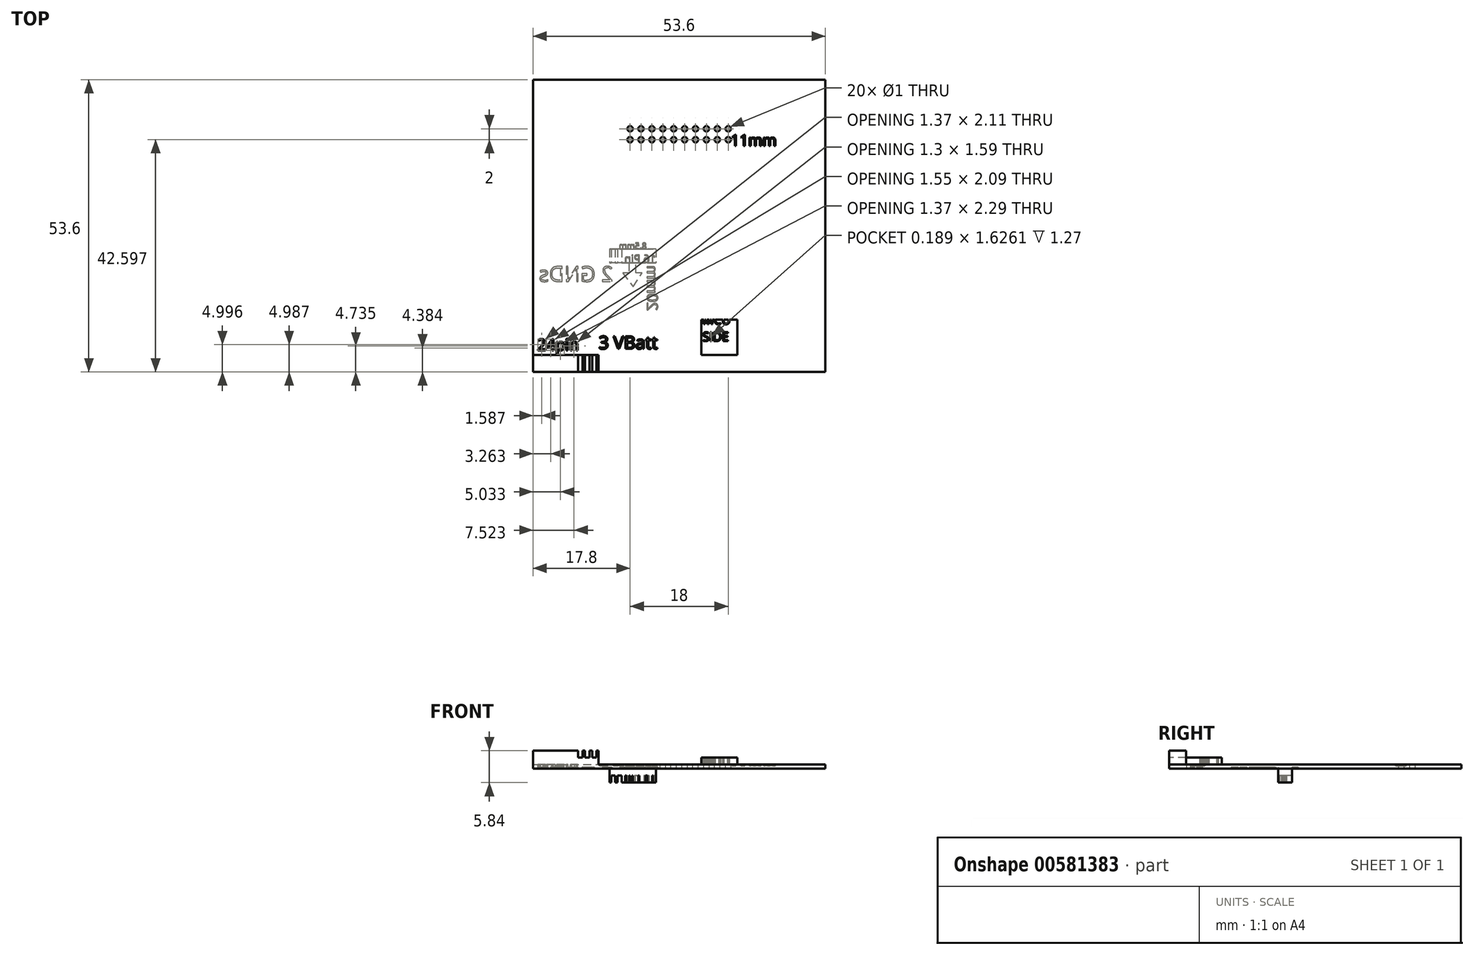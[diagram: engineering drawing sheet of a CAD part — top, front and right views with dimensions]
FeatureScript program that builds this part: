
annotation { "Feature Type Name" : "Feature", "Feature Type Description" : "" }
export const myFeature = defineFeature(function(context is Context, id is Id, definition is map)
    precondition{}
    {
        {
            var Q0;
            Q0=qCreatedBy(makeId("Top.planeOp"),FACE);
            var sketch = newSketch(context, id + "F0", { "sketchPlane" : qUnion([Q0])});
            skLineSegment(sketch, "E0.bottom", {"start": v(-26.8, 26.8) * mm, "end": v(26.8, 26.8) * mm});
            skLineSegment(sketch, "E0.top", {"start": v(-26.8, -26.8) * mm, "end": v(26.8, -26.8) * mm});
            skLineSegment(sketch, "E0.left", {"start": v(-26.8, 26.8) * mm, "end": v(-26.8, -26.8) * mm});
            skLineSegment(sketch, "E0.right", {"start": v(26.8, 26.8) * mm, "end": v(26.8, -26.8) * mm});
            skPoint(sketch, "E0.middle", {"position": v(0, 0) * mm});
            skSolve(sketch);
        }
        {
            var Q0;
            Q0 = qSketchRegion(id + "F0", true);
            extrude(context, id + "F1", {"entities" : qUnion([Q0]), "depth" : 0.76 * mm, "offsetDistance" : 25.4 * mm});
        }
        {
            var Q0;
            Q0=makeQuery(id+"F1.opExtrude","CAP_FACE",FACE,{"disambiguationData":[OSD([sQuery(id+"F0.wireOp",EDGE,"E0.bottom"),sQuery(id+"F0.wireOp",EDGE,"E0.top"),sQuery(id+"F0.wireOp",EDGE,"E0.left"),sQuery(id+"F0.wireOp",EDGE,"E0.right")])],"isStart":false});
            var sketch = newSketch(context, id + "F2", { "sketchPlane" : qUnion([Q0])});
            skPoint(sketch, "E1.middle.positionSnap0", {"position": v(0, 26.8) * mm});
            skPoint(sketch, "E1.centerSnap0", {"position": v(0, 26.8) * mm});
            skCircle(sketch, "E2", {"center": v(-9, 15.8) * mm, "radius": 0.5 * mm});
            skCircle(sketch, "E3.0.1.0", {"center": v(-9, 17.8) * mm, "radius": 0.5 * mm});
            skCircle(sketch, "E3.1.0.0", {"center": v(-7, 15.8) * mm, "radius": 0.5 * mm});
            skCircle(sketch, "E3.1.1.0", {"center": v(-7, 17.8) * mm, "radius": 0.5 * mm});
            skCircle(sketch, "E3.2.0.0", {"center": v(-5, 15.8) * mm, "radius": 0.5 * mm});
            skCircle(sketch, "E3.2.1.0", {"center": v(-5, 17.8) * mm, "radius": 0.5 * mm});
            skCircle(sketch, "E3.3.0.0", {"center": v(-3, 15.8) * mm, "radius": 0.5 * mm});
            skCircle(sketch, "E3.3.1.0", {"center": v(-3, 17.8) * mm, "radius": 0.5 * mm});
            skCircle(sketch, "E3.4.0.0", {"center": v(-1, 15.8) * mm, "radius": 0.5 * mm});
            skCircle(sketch, "E3.4.1.0", {"center": v(-1, 17.8) * mm, "radius": 0.5 * mm});
            skCircle(sketch, "E3.5.0.0", {"center": v(1, 15.8) * mm, "radius": 0.5 * mm});
            skCircle(sketch, "E3.5.1.0", {"center": v(1, 17.8) * mm, "radius": 0.5 * mm});
            skCircle(sketch, "E3.6.0.0", {"center": v(3, 15.8) * mm, "radius": 0.5 * mm});
            skCircle(sketch, "E3.6.1.0", {"center": v(3, 17.8) * mm, "radius": 0.5 * mm});
            skCircle(sketch, "E3.7.0.0", {"center": v(5, 15.8) * mm, "radius": 0.5 * mm});
            skCircle(sketch, "E3.7.1.0", {"center": v(5, 17.8) * mm, "radius": 0.5 * mm});
            skCircle(sketch, "E3.8.0.0", {"center": v(7, 15.8) * mm, "radius": 0.5 * mm});
            skCircle(sketch, "E3.8.1.0", {"center": v(7, 17.8) * mm, "radius": 0.5 * mm});
            skCircle(sketch, "E3.9.0.0", {"center": v(9, 15.8) * mm, "radius": 0.5 * mm});
            skCircle(sketch, "E3.9.1.0", {"center": v(9, 17.8) * mm, "radius": 0.5 * mm});
            skLineSegment(sketch, "E3.direction1", {"start": v(-9, 15.8) * mm, "end": v(-7, 15.8) * mm, "construction": true});
            skLineSegment(sketch, "E3.direction2", {"start": v(-9, 15.8) * mm, "end": v(-9, 17.8) * mm, "construction": true});
            skSolve(sketch);
        }
        {
            var Q0;
            Q0 = qSketchRegion(id + "F2", true);
            extrude(context, id + "F3", {"entities" : qUnion([Q0]), "operationType" : NewBodyOperationType.REMOVE, "oppositeDirection" : true, "depth" : 25.4 * mm, "offsetDistance" : 25.4 * mm});
        }
        {
            var Q0;
            Q0=makeQuery(id+"F1.opExtrude","CAP_FACE",FACE,{"disambiguationData":[OSD([sQuery(id+"F0.wireOp",EDGE,"E0.bottom"),sQuery(id+"F0.wireOp",EDGE,"E0.top"),sQuery(id+"F0.wireOp",EDGE,"E0.left"),sQuery(id+"F0.wireOp",EDGE,"E0.right")])],"isStart":false});
            var sketch = newSketch(context, id + "F4", { "sketchPlane" : qUnion([Q0])});
            skLineSegment(sketch, "E4.bottom", {"start": v(-26.8, -23.69) * mm, "end": v(-14.8, -23.69) * mm});
            skLineSegment(sketch, "E4.top", {"start": v(-26.8, -26.8) * mm, "end": v(-14.8, -26.8) * mm});
            skLineSegment(sketch, "E4.left", {"start": v(-26.8, -23.69) * mm, "end": v(-26.8, -26.8) * mm});
            skLineSegment(sketch, "E4.right", {"start": v(-14.8, -23.69) * mm, "end": v(-14.8, -26.8) * mm});
            skLineSegment(sketch, "E5", {"start": v(-20.8, -23.69) * mm, "end": v(-20.8, -26.8) * mm, "construction": true});
            skSolve(sketch);
        }
        {
            var Q0;
            Q0 = qSketchRegion(id + "F4", true);
            extrude(context, id + "F5", {"entities" : qUnion([Q0]), "operationType" : NewBodyOperationType.ADD, "depth" : 2.54 * mm, "offsetDistance" : 25.4 * mm});
        }
        {
            var Q0;
            Q0=makeQuery(id+"F1.opExtrude","CAP_FACE",FACE,{"disambiguationData":[OSD([sQuery(id+"F0.wireOp",EDGE,"E0.bottom"),sQuery(id+"F0.wireOp",EDGE,"E0.top"),sQuery(id+"F0.wireOp",EDGE,"E0.left"),sQuery(id+"F0.wireOp",EDGE,"E0.right")])],"isStart":false});
            var sketch = newSketch(context, id + "F6", { "sketchPlane" : qUnion([Q0])});
            skText(sketch, "E6", { "text": "24pin", "fontName": "OpenSans-Regular.ttf"});
            const initialGuessF6  = {"E6": [-0.02604, -0.02286, 1, 0, 0.0021]};
            skSetInitialGuess(sketch, initialGuessF6);
            skSolve(sketch);
        }
        {
            var Q0;
            Q0 = qSketchRegion(id + "F6", true);
            extrude(context, id + "F7", {"entities" : qUnion([Q0]), "operationType" : NewBodyOperationType.REMOVE, "oppositeDirection" : true, "depth" : 1.27 * mm, "offsetDistance" : 25.4 * mm});
        }
        {
            var Q0;
            Q0=makeQuery(id+"F1.opExtrude","CAP_FACE",FACE,{"disambiguationData":[OSD([sQuery(id+"F0.wireOp",EDGE,"E0.bottom"),sQuery(id+"F0.wireOp",EDGE,"E0.top"),sQuery(id+"F0.wireOp",EDGE,"E0.left"),sQuery(id+"F0.wireOp",EDGE,"E0.right")])],"isStart":false});
            var sketch = newSketch(context, id + "F8", { "sketchPlane" : qUnion([Q0])});
            skLineSegment(sketch, "E7.bottom", {"start": v(10.68, -23.69) * mm, "end": v(4.08, -23.69) * mm});
            skLineSegment(sketch, "E7.top", {"start": v(10.68, -17.2) * mm, "end": v(4.08, -17.2) * mm});
            skLineSegment(sketch, "E7.left", {"start": v(10.68, -23.69) * mm, "end": v(10.68, -17.2) * mm});
            skLineSegment(sketch, "E7.right", {"start": v(4.08, -23.69) * mm, "end": v(4.08, -17.2) * mm});
            skSolve(sketch);
        }
        {
            var Q0;
            Q0 = qSketchRegion(id + "F8", true);
            extrude(context, id + "F9", {"entities" : qUnion([Q0]), "operationType" : NewBodyOperationType.ADD, "depth" : 1.27 * mm, "offsetDistance" : 25.4 * mm});
        }
        {
            var Q0;
            Q0=makeQuery(id+"F9.opExtrude","CAP_FACE",FACE,{"disambiguationData":[OSD([sQuery(id+"F8.wireOp",EDGE,"E7.bottom"),sQuery(id+"F8.wireOp",EDGE,"E7.top"),sQuery(id+"F8.wireOp",EDGE,"E7.left"),sQuery(id+"F8.wireOp",EDGE,"E7.right")])],"isStart":false});
            var sketch = newSketch(context, id + "F10", { "sketchPlane" : qUnion([Q0])});
            skText(sketch, "E8", { "text": "MCU\nSIDE", "fontName": "OpenSans-Regular.ttf"});
            const initialGuessF10  = {"E8": [0.00427, -0.01806, 1, 0, 0.00164]};
            skSetInitialGuess(sketch, initialGuessF10);
            skSolve(sketch);
        }
        {
            var Q0;
            Q0 = qSketchRegion(id + "F10", true);
            extrude(context, id + "F11", {"entities" : qUnion([Q0]), "operationType" : NewBodyOperationType.REMOVE, "oppositeDirection" : true, "depth" : 1.27 * mm, "offsetDistance" : 25.4 * mm});
        }
        {
            var Q0;
            Q0=makeQuery(id+"F1.opExtrude","CAP_FACE",FACE,{"disambiguationData":[OSD([sQuery(id+"F0.wireOp",EDGE,"E0.bottom"),sQuery(id+"F0.wireOp",EDGE,"E0.top"),sQuery(id+"F0.wireOp",EDGE,"E0.left"),sQuery(id+"F0.wireOp",EDGE,"E0.right")])],"isStart":true});
            var sketch = newSketch(context, id + "F12", { "sketchPlane" : qUnion([Q0])});
            skLineSegment(sketch, "E9.bottom", {"start": v(-4.25, 4.26) * mm, "end": v(-12.75, 4.26) * mm});
            skLineSegment(sketch, "E9.top", {"start": v(-4.25, 6.8) * mm, "end": v(-12.75, 6.8) * mm});
            skLineSegment(sketch, "E9.left", {"start": v(-4.25, 4.26) * mm, "end": v(-4.25, 6.8) * mm});
            skLineSegment(sketch, "E9.right", {"start": v(-12.75, 4.26) * mm, "end": v(-12.75, 6.8) * mm});
            skLineSegment(sketch, "E10", {"start": v(-4.25, 5.53) * mm, "end": v(-8.5, 4.26) * mm, "construction": true});
            skLineSegment(sketch, "E11", {"start": v(0, 0) * mm, "end": v(0, 26.8) * mm, "construction": true});
            skSolve(sketch);
        }
        {
            var Q0;
            Q0 = qSketchRegion(id + "F12", true);
            extrude(context, id + "F13", {"entities" : qUnion([Q0]), "operationType" : NewBodyOperationType.ADD, "depth" : 2.54 * mm, "offsetDistance" : 25.4 * mm});
        }
        {
            var Q0;
            Q0=makeQuery(id+"F13.opExtrude","CAP_FACE",FACE,{"disambiguationData":[OSD([sQuery(id+"F12.wireOp",EDGE,"E9.bottom"),sQuery(id+"F12.wireOp",EDGE,"E9.top"),sQuery(id+"F12.wireOp",EDGE,"E9.left"),sQuery(id+"F12.wireOp",EDGE,"E9.right")])],"isStart":false});
            var sketch = newSketch(context, id + "F14", { "sketchPlane" : qUnion([Q0])});
            skText(sketch, "E12", { "text": "16 Pin", "fontName": "OpenSans-Regular.ttf"});
            skLineSegment(sketch, "E13.bottom", {"start": v(-12.48, 4.26) * mm, "end": v(-11.72, 4.26) * mm});
            skLineSegment(sketch, "E13.top", {"start": v(-12.48, 6.8) * mm, "end": v(-11.72, 6.8) * mm});
            skLineSegment(sketch, "E13.left", {"start": v(-12.48, 4.26) * mm, "end": v(-12.48, 6.8) * mm});
            skLineSegment(sketch, "E13.right", {"start": v(-11.72, 4.26) * mm, "end": v(-11.72, 6.8) * mm});
            skLineSegment(sketch, "E14.bottom", {"start": v(-11.33, 4.26) * mm, "end": v(-10.57, 4.26) * mm});
            skLineSegment(sketch, "E14.top", {"start": v(-11.33, 6.8) * mm, "end": v(-10.57, 6.8) * mm});
            skLineSegment(sketch, "E14.left", {"start": v(-11.33, 4.26) * mm, "end": v(-11.33, 6.8) * mm});
            skLineSegment(sketch, "E14.right", {"start": v(-10.57, 4.26) * mm, "end": v(-10.57, 6.8) * mm});
            const initialGuessF14  = {"E12": [-0.00425, 0.0068, -1, 0, 0.00146]};
            skSetInitialGuess(sketch, initialGuessF14);
            skSolve(sketch);
        }
        {
            var Q0;
            Q0 = qSketchRegion(id + "F14", true);
            extrude(context, id + "F15", {"entities" : qUnion([Q0]), "operationType" : NewBodyOperationType.REMOVE, "oppositeDirection" : true, "depth" : 1.27 * mm, "offsetDistance" : 25.4 * mm});
        }
        {
            var Q0;
            {var subQ0=sQuery(id+"F0.wireOp",EDGE,"E0.left");var subQ1=sQuery(id+"F0.wireOp",EDGE,"E0.top");var subQ2=sQuery(id+"F0.wireOp",EDGE,"E0.right");var subQ3=sQuery(id+"F0.wireOp",EDGE,"E0.bottom");Q0=makeQuery(id+"F7.boolean.opBoolean","SPLIT",FACE,{"disambiguationData":[TD([makeQuery(id+"F1.opExtrude","SWEPT_FACE",FACE,{"disambiguationData":[OSD([subQ3])]})])],"derivedFrom":makeQuery(id+"F1.opExtrude","CAP_FACE",FACE,{"disambiguationData":[OSD([subQ3,subQ1,subQ0,subQ2])],"isStart":true})});}
            var sketch = newSketch(context, id + "F16", { "sketchPlane" : qUnion([Q0])});
            skLineSegment(sketch, "E15", {"start": v(-7.95, 8.63) * mm, "end": v(-7.95, 6.8) * mm});
            skLineSegment(sketch, "E16", {"start": v(-7.95, 6.8) * mm, "end": v(-9.21, 6.8) * mm});
            skLineSegment(sketch, "E17", {"start": v(-9.21, 6.8) * mm, "end": v(-9.21, 8.63) * mm});
            skLineSegment(sketch, "E18", {"start": v(-9.21, 8.63) * mm, "end": v(-10.35, 8.63) * mm});
            skLineSegment(sketch, "E19", {"start": v(-10.35, 8.63) * mm, "end": v(-8.45, 11.16) * mm});
            skLineSegment(sketch, "E20", {"start": v(-8.45, 11.16) * mm, "end": v(-6.8, 8.63) * mm});
            skLineSegment(sketch, "E21", {"start": v(-6.8, 8.63) * mm, "end": v(-7.95, 8.63) * mm});
            skSolve(sketch);
        }
        {
            var Q0;
            Q0 = qSketchRegion(id + "F16", true);
            extrude(context, id + "F17", {"entities" : qUnion([Q0]), "operationType" : NewBodyOperationType.REMOVE, "oppositeDirection" : true, "depth" : 0.25 * mm, "offsetDistance" : 25.4 * mm});
        }
        {
            var Q0;
            {var subQ0=sQuery(id+"F0.wireOp",EDGE,"E0.left");var subQ1=sQuery(id+"F0.wireOp",EDGE,"E0.top");var subQ2=sQuery(id+"F0.wireOp",EDGE,"E0.right");var subQ3=sQuery(id+"F0.wireOp",EDGE,"E0.bottom");Q0=makeQuery(id+"F7.boolean.opBoolean","SPLIT",FACE,{"disambiguationData":[TD([makeQuery(id+"F1.opExtrude","SWEPT_FACE",FACE,{"disambiguationData":[OSD([subQ3])]})])],"derivedFrom":makeQuery(id+"F1.opExtrude","CAP_FACE",FACE,{"disambiguationData":[OSD([subQ3,subQ1,subQ0,subQ2])],"isStart":true})});}
            var sketch = newSketch(context, id + "F18", { "sketchPlane" : qUnion([Q0])});
            skText(sketch, "E22", { "text": "2 GNDs", "fontName": "OpenSans-Regular.ttf"});
            const initialGuessF18  = {"E22": [-0.0121, 0.01023, -1, 0, 0.00279]};
            skSetInitialGuess(sketch, initialGuessF18);
            skSolve(sketch);
        }
        {
            var Q0;
            Q0 = qSketchRegion(id + "F18", true);
            extrude(context, id + "F19", {"entities" : qUnion([Q0]), "operationType" : NewBodyOperationType.REMOVE, "oppositeDirection" : true, "depth" : 0.25 * mm, "offsetDistance" : 25.4 * mm});
        }
        {
            var Q0;
            Q0=makeQuery(id+"F5.opExtrude","CAP_FACE",FACE,{"disambiguationData":[OSD([sQuery(id+"F4.wireOp",EDGE,"E4.bottom"),sQuery(id+"F4.wireOp",EDGE,"E4.top"),sQuery(id+"F4.wireOp",EDGE,"E4.left"),sQuery(id+"F4.wireOp",EDGE,"E4.right")])],"isStart":false});
            var sketch = newSketch(context, id + "F20", { "sketchPlane" : qUnion([Q0])});
            skLineSegment(sketch, "E23.bottom", {"start": v(-15.15, -23.69) * mm, "end": v(-15.96, -23.69) * mm});
            skLineSegment(sketch, "E23.top", {"start": v(-15.15, -26.8) * mm, "end": v(-15.96, -26.8) * mm});
            skLineSegment(sketch, "E23.left", {"start": v(-15.15, -23.69) * mm, "end": v(-15.15, -26.8) * mm});
            skLineSegment(sketch, "E23.right", {"start": v(-15.96, -23.69) * mm, "end": v(-15.96, -26.8) * mm});
            skLineSegment(sketch, "E24.bottom", {"start": v(-16.45, -23.69) * mm, "end": v(-17.26, -23.69) * mm});
            skLineSegment(sketch, "E24.top", {"start": v(-16.45, -26.8) * mm, "end": v(-17.26, -26.8) * mm});
            skLineSegment(sketch, "E24.left", {"start": v(-16.45, -23.69) * mm, "end": v(-16.45, -26.8) * mm});
            skLineSegment(sketch, "E24.right", {"start": v(-17.26, -23.69) * mm, "end": v(-17.26, -26.8) * mm});
            skLineSegment(sketch, "E25.bottom", {"start": v(-17.75, -23.69) * mm, "end": v(-18.55, -23.69) * mm});
            skLineSegment(sketch, "E25.top", {"start": v(-17.75, -26.8) * mm, "end": v(-18.55, -26.8) * mm});
            skLineSegment(sketch, "E25.left", {"start": v(-17.75, -23.69) * mm, "end": v(-17.75, -26.8) * mm});
            skLineSegment(sketch, "E25.right", {"start": v(-18.55, -23.69) * mm, "end": v(-18.55, -26.8) * mm});
            skLineSegment(sketch, "E26", {"start": v(-17.75, -24.75) * mm, "end": v(-17.26, -24.75) * mm, "construction": true});
            skLineSegment(sketch, "E27", {"start": v(-17.26, -24.75) * mm, "end": v(-16.45, -24.75) * mm, "construction": true});
            skLineSegment(sketch, "E28", {"start": v(-16.45, -24.75) * mm, "end": v(-15.96, -24.75) * mm, "construction": true});
            skSolve(sketch);
        }
        {
            var Q0;
            Q0 = qSketchRegion(id + "F20", true);
            extrude(context, id + "F21", {"entities" : qUnion([Q0]), "operationType" : NewBodyOperationType.REMOVE, "oppositeDirection" : true, "depth" : 1.27 * mm, "offsetDistance" : 25.4 * mm});
        }
        {
            var Q0;
            {var subQ0=sQuery(id+"F0.wireOp",EDGE,"E0.left");var subQ1=sQuery(id+"F0.wireOp",EDGE,"E0.top");var subQ2=sQuery(id+"F0.wireOp",EDGE,"E0.right");var subQ3=sQuery(id+"F0.wireOp",EDGE,"E0.bottom");Q0=makeQuery(id+"F11.boolean.opBoolean","MERGE",FACE,{"derivedFrom":[makeQuery(id+"F7.boolean.opBoolean","SPLIT",FACE,{"disambiguationData":[TD([makeQuery(id+"F1.opExtrude","SWEPT_FACE",FACE,{"disambiguationData":[OSD([subQ3])]})])],"derivedFrom":makeQuery(id+"F1.opExtrude","CAP_FACE",FACE,{"disambiguationData":[OSD([subQ3,subQ1,subQ0,subQ2])],"isStart":false})}),makeQuery(id+"F11.opExtrude","CAP_FACE",FACE,{"disambiguationData":[OSD([sQuery(id+"F10.wireOp",EDGE,"E8.sketch_text.stroke-18"),sQuery(id+"F10.wireOp",EDGE,"E8.sketch_text.stroke-19"),sQuery(id+"F10.wireOp",EDGE,"E8.sketch_text.stroke-20"),sQuery(id+"F10.wireOp",EDGE,"E8.sketch_text.stroke-21"),sQuery(id+"F10.wireOp",EDGE,"E8.sketch_text.stroke-22"),sQuery(id+"F10.wireOp",EDGE,"E8.sketch_text.stroke-23"),sQuery(id+"F10.wireOp",EDGE,"E8.sketch_text.stroke-24"),sQuery(id+"F10.wireOp",EDGE,"E8.sketch_text.stroke-25"),sQuery(id+"F10.wireOp",EDGE,"E8.sketch_text.stroke-26"),sQuery(id+"F10.wireOp",EDGE,"E8.sketch_text.stroke-27"),sQuery(id+"F10.wireOp",EDGE,"E8.sketch_text.stroke-28"),sQuery(id+"F10.wireOp",EDGE,"E8.sketch_text.stroke-29"),sQuery(id+"F10.wireOp",EDGE,"E8.sketch_text.stroke-30"),sQuery(id+"F10.wireOp",EDGE,"E8.sketch_text.stroke-31"),sQuery(id+"F10.wireOp",EDGE,"E8.sketch_text.stroke-32")])],"isStart":false})]});}
            var sketch = newSketch(context, id + "F22", { "sketchPlane" : qUnion([Q0])});
            skText(sketch, "E29", { "text": "3 VBatt", "fontName": "OpenSans-Regular.ttf"});
            const initialGuessF22  = {"E29": [-0.01477, -0.02258, 1, 0, 0.00234]};
            skSetInitialGuess(sketch, initialGuessF22);
            skSolve(sketch);
        }
        {
            var Q0;
            Q0 = qSketchRegion(id + "F22", true);
            extrude(context, id + "F23", {"entities" : qUnion([Q0]), "operationType" : NewBodyOperationType.REMOVE, "oppositeDirection" : true, "depth" : 0.25 * mm, "offsetDistance" : 25.4 * mm});
        }
        {
            var Q0;
            {var subQ23=sQuery(id+"F10.wireOp",EDGE,"E8.sketch_text.stroke-32");var subQ24=sQuery(id+"F10.wireOp",EDGE,"E8.sketch_text.stroke-31");var subQ25=sQuery(id+"F10.wireOp",EDGE,"E8.sketch_text.stroke-30");var subQ26=sQuery(id+"F10.wireOp",EDGE,"E8.sketch_text.stroke-29");var subQ27=sQuery(id+"F10.wireOp",EDGE,"E8.sketch_text.stroke-28");var subQ28=sQuery(id+"F10.wireOp",EDGE,"E8.sketch_text.stroke-27");var subQ29=sQuery(id+"F10.wireOp",EDGE,"E8.sketch_text.stroke-26");var subQ30=sQuery(id+"F10.wireOp",EDGE,"E8.sketch_text.stroke-25");var subQ31=sQuery(id+"F10.wireOp",EDGE,"E8.sketch_text.stroke-24");var subQ32=sQuery(id+"F10.wireOp",EDGE,"E8.sketch_text.stroke-23");var subQ33=sQuery(id+"F10.wireOp",EDGE,"E8.sketch_text.stroke-19");var subQ34=sQuery(id+"F10.wireOp",EDGE,"E8.sketch_text.stroke-18");var subQ74=sQuery(id+"F0.wireOp",EDGE,"E0.bottom");var subQ75=makeQuery(id+"F1.opExtrude","SWEPT_FACE",FACE,{"disambiguationData":[OSD([subQ74])]});var subQ79=sQuery(id+"F10.wireOp",EDGE,"E8.sketch_text.stroke-22");var subQ80=sQuery(id+"F0.wireOp",EDGE,"E0.right");var subQ85=sQuery(id+"F10.wireOp",EDGE,"E8.sketch_text.stroke-20");var subQ86=sQuery(id+"F0.wireOp",EDGE,"E0.top");var subQ90=sQuery(id+"F10.wireOp",EDGE,"E8.sketch_text.stroke-21");var subQ91=sQuery(id+"F0.wireOp",EDGE,"E0.left");Q0=makeQuery(id+"F23.boolean.opBoolean","SPLIT",FACE,{"disambiguationData":[TD([subQ75])],"derivedFrom":makeQuery(id+"F11.boolean.opBoolean","MERGE",FACE,{"derivedFrom":[makeQuery(id+"F7.boolean.opBoolean","SPLIT",FACE,{"disambiguationData":[TD([subQ75])],"derivedFrom":makeQuery(id+"F1.opExtrude","CAP_FACE",FACE,{"disambiguationData":[OSD([subQ74,subQ86,subQ91,subQ80])],"isStart":false})}),makeQuery(id+"F11.opExtrude","CAP_FACE",FACE,{"disambiguationData":[OSD([subQ34,subQ33,subQ85,subQ90,subQ79,subQ32,subQ31,subQ30,subQ29,subQ28,subQ27,subQ26,subQ25,subQ24,subQ23])],"isStart":false})]})});}
            var sketch = newSketch(context, id + "F24", { "sketchPlane" : qUnion([Q0])});
            skLineSegment(sketch, "E30.bottom", {"start": v(10.58, 26.8) * mm, "end": v(11.18, 26.8) * mm, "construction": true});
            skLineSegment(sketch, "E30.top", {"start": v(10.58, 15.8) * mm, "end": v(11.18, 15.8) * mm, "construction": true});
            skLineSegment(sketch, "E30.left", {"start": v(10.58, 26.8) * mm, "end": v(10.58, 15.8) * mm, "construction": true});
            skLineSegment(sketch, "E30.right", {"start": v(11.18, 26.8) * mm, "end": v(11.18, 15.8) * mm, "construction": true});
            skLineSegment(sketch, "E31", {"start": v(9, 15.8) * mm, "end": v(9, 17.8) * mm, "construction": true});
            skText(sketch, "E32", { "text": "11mm", "fontName": "OpenSans-Regular.ttf"});
            const initialGuessF24  = {"E32": [0.00947, 0.01469, 1, 0, 0.00201]};
            skSetInitialGuess(sketch, initialGuessF24);
            skSolve(sketch);
        }
        {
            var Q0;
            Q0 = qSketchRegion(id + "F24", true);
            extrude(context, id + "F25", {"entities" : qUnion([Q0]), "operationType" : NewBodyOperationType.REMOVE, "oppositeDirection" : true, "depth" : 0.25 * mm, "offsetDistance" : 25.4 * mm});
        }
        {
            var Q0;
            {var subQ43=sQuery(id+"F0.wireOp",EDGE,"E0.bottom");var subQ44=makeQuery(id+"F1.opExtrude","SWEPT_FACE",FACE,{"disambiguationData":[OSD([subQ43])]});var subQ48=sQuery(id+"F0.wireOp",EDGE,"E0.right");var subQ55=sQuery(id+"F0.wireOp",EDGE,"E0.top");var subQ60=sQuery(id+"F0.wireOp",EDGE,"E0.left");Q0=makeQuery(id+"F19.boolean.opBoolean","SPLIT",FACE,{"disambiguationData":[TD([subQ44])],"derivedFrom":makeQuery(id+"F7.boolean.opBoolean","SPLIT",FACE,{"disambiguationData":[TD([subQ44])],"derivedFrom":makeQuery(id+"F1.opExtrude","CAP_FACE",FACE,{"disambiguationData":[OSD([subQ43,subQ55,subQ60,subQ48])],"isStart":true})})});}
            var sketch = newSketch(context, id + "F26", { "sketchPlane" : qUnion([Q0])});
            skText(sketch, "E33", { "text": "8.5mm", "fontName": "OpenSans-Regular.ttf"});
            skText(sketch, "E34", { "text": "20mm", "fontName": "OpenSans-Regular.ttf"});
            const initialGuessF26  = {"E33": [-0.00596, 0.00426, -1, 0, 0.00112], "E34": [-0.0059, 0.01559, 0, -1, 0.002]};
            skSetInitialGuess(sketch, initialGuessF26);
            skSolve(sketch);
        }
        {
            var Q0;
            Q0 = qSketchRegion(id + "F26", true);
            extrude(context, id + "F27", {"entities" : qUnion([Q0]), "operationType" : NewBodyOperationType.REMOVE, "oppositeDirection" : true, "depth" : 0.25 * mm, "offsetDistance" : 25.4 * mm});
        }
    });
